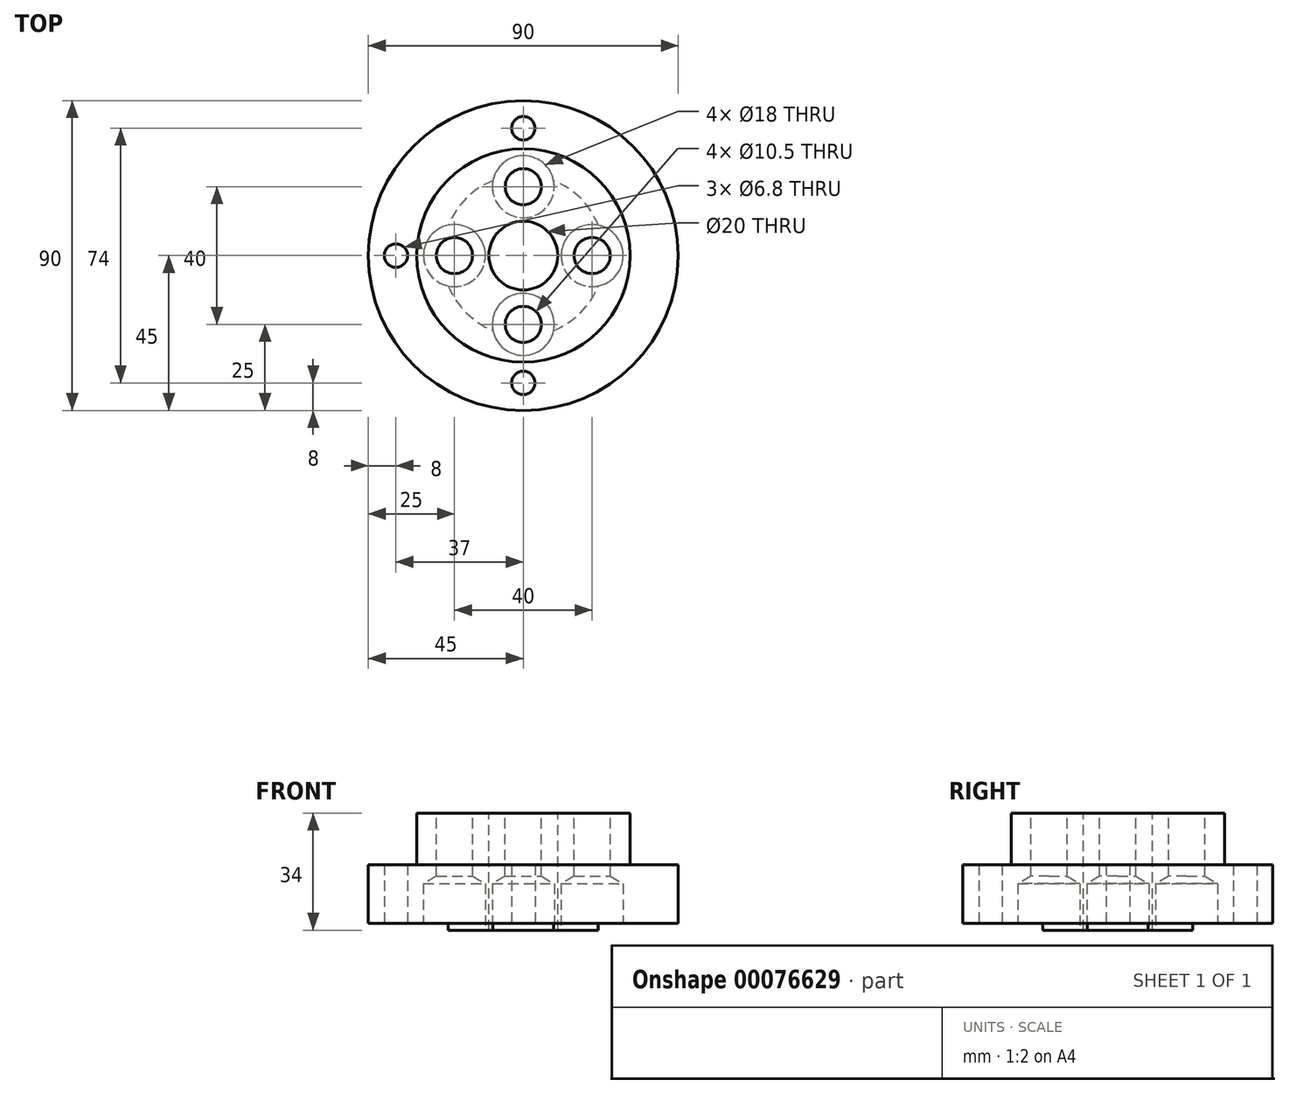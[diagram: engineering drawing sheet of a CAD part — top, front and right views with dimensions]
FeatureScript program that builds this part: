
annotation { "Feature Type Name" : "Feature", "Feature Type Description" : "" }
export const myFeature = defineFeature(function(context is Context, id is Id, definition is map)
    precondition{}
    {
        {
            var Q0;
            Q0=qCreatedBy(makeId("Top.planeOp"),FACE);
            var sketch = newSketch(context, id + "F0", { "sketchPlane" : qUnion([Q0])});
            skCircle(sketch, "E0", {"center": v(0, 0) * mm, "radius": 45 * mm});
            skSolve(sketch);
        }
        {
            var Q0;
            Q0=qSketchRegion(id+"F0",true);
            extrude(context, id + "F1", {"entities" : qUnion([Q0]), "depth" : 17 * mm});
        }
        {
            var Q0;
            Q0=makeQuery(id+"F1.opExtrude","CAP_FACE",FACE,{"disambiguationData":[OSD([sQuery(id+"F0.wireOp",EDGE,"E0")])],"isStart":false});
            var sketch = newSketch(context, id + "F2", { "sketchPlane" : qUnion([Q0])});
            skCircle(sketch, "E1", {"center": v(0, 0) * mm, "radius": 31 * mm});
            skSolve(sketch);
        }
        {
            var Q0;
            Q0=qSketchRegion(id+"F2",true);
            extrude(context, id + "F3", {"entities" : qUnion([Q0]), "operationType" : NewBodyOperationType.ADD, "depth" : 15 * mm});
        }
        {
            var Q0;
            Q0=makeQuery(id+"F3.opExtrude","CAP_FACE",FACE,{"disambiguationData":[OSD([sQuery(id+"F2.wireOp",EDGE,"E1")])],"isStart":false});
            var sketch = newSketch(context, id + "F4", { "sketchPlane" : qUnion([Q0])});
            skCircle(sketch, "E2", {"center": v(0, 0) * mm, "radius": 10 * mm});
            skSolve(sketch);
        }
        {
            var Q0;
            Q0=makeQuery(id+"F3.opExtrude","CAP_FACE",FACE,{"disambiguationData":[OSD([sQuery(id+"F2.wireOp",EDGE,"E1")])],"isStart":false});
            var sketch = newSketch(context, id + "F5", { "sketchPlane" : qUnion([Q0])});
            skCircle(sketch, "E3", {"center": v(20, 0) * mm, "radius": 5.25 * mm});
            skCircle(sketch, "E4", {"center": v(0, -20) * mm, "radius": 5.25 * mm});
            skCircle(sketch, "E5", {"center": v(-20, 0) * mm, "radius": 5.25 * mm});
            skCircle(sketch, "E6", {"center": v(0, 20) * mm, "radius": 5.25 * mm});
            skSolve(sketch);
        }
        {
            var Q0;
            Q0=makeQuery(id+"F1.opExtrude","CAP_FACE",FACE,{"disambiguationData":[OSD([sQuery(id+"F0.wireOp",EDGE,"E0")])],"isStart":true});
            var sketch = newSketch(context, id + "F6", { "sketchPlane" : qUnion([Q0])});
            skCircle(sketch, "E7", {"center": v(0, 0) * mm, "radius": 23.5 * mm});
            skSolve(sketch);
        }
        {
            var Q0;
            Q0=qSketchRegion(id+"F6",true);
            extrude(context, id + "F7", {"entities" : qUnion([Q0]), "operationType" : NewBodyOperationType.ADD, "depth" : 2 * mm});
        }
        {
            var Q0;
            Q0=makeQuery(id+"F7.opExtrude","CAP_FACE",FACE,{"disambiguationData":[OSD([sQuery(id+"F6.wireOp",EDGE,"E7")])],"isStart":false});
            var sketch = newSketch(context, id + "F8", { "sketchPlane" : qUnion([Q0])});
            skCircle(sketch, "E8", {"center": v(0, 20) * mm, "radius": 9 * mm});
            skCircle(sketch, "E9", {"center": v(20, 0) * mm, "radius": 9 * mm});
            skCircle(sketch, "E10", {"center": v(0, -20) * mm, "radius": 9 * mm});
            skCircle(sketch, "E11", {"center": v(-20, 0) * mm, "radius": 9 * mm});
            skSolve(sketch);
        }
        {
            var Q0;
            Q0=sQuery(id+"F8.wireOp",VERTEX,"E11.center");
            var Q1;
            Q1=sQuery(id+"F8.wireOp",VERTEX,"E8.center");
            var Q2;
            Q2=sQuery(id+"F8.wireOp",VERTEX,"E9.center");
            var Q3;
            Q3=sQuery(id+"F8.wireOp",VERTEX,"E10.center");
            var Q4;
            Q4=makeQuery(id+"F1.opExtrude","SWEPT_BODY",BODY,{"disambiguationData":[OSD([sQuery(id+"F0.wireOp",EDGE,"E0")])]});
            hole(context, id + "F9", {"style" : HoleStyle.SIMPLE, "endStyle" : HoleEndStyle.BLIND, "holeDiameter" : 18 * mm, "holeDepth" : 13.5 * mm, "startFromSketch" : true, "locations" : qUnion([Q0, Q1, Q2, Q3]), "scope" : qUnion([Q4])});
        }
        {
            var Q0;
            Q0=sQuery(id+"F4.wireOp",VERTEX,"E2.center");
            var Q1;
            Q1=makeQuery(id+"F1.opExtrude","SWEPT_BODY",BODY,{"disambiguationData":[OSD([sQuery(id+"F0.wireOp",EDGE,"E0")])]});
            hole(context, id + "F10", {"style" : HoleStyle.SIMPLE, "endStyle" : HoleEndStyle.THROUGH, "holeDiameter" : 20 * mm, "startFromSketch" : true, "locations" : qUnion([Q0]), "scope" : qUnion([Q1]), "isTappedThrough" : true});
        }
        {
            var Q0;
            Q0=sQuery(id+"F5.wireOp",VERTEX,"E5.center");
            var Q1;
            Q1=sQuery(id+"F5.wireOp",VERTEX,"E6.center");
            var Q2;
            Q2=sQuery(id+"F5.wireOp",VERTEX,"E3.center");
            var Q3;
            Q3=sQuery(id+"F5.wireOp",VERTEX,"E4.center");
            var Q4;
            Q4=makeQuery(id+"F1.opExtrude","SWEPT_BODY",BODY,{"disambiguationData":[OSD([sQuery(id+"F0.wireOp",EDGE,"E0")])]});
            hole(context, id + "F11", {"style" : HoleStyle.SIMPLE, "endStyle" : HoleEndStyle.THROUGH, "holeDiameter" : 10.5 * mm, "startFromSketch" : true, "locations" : qUnion([Q0, Q1, Q2, Q3]), "scope" : qUnion([Q4]), "isTappedThrough" : true});
        }
        {
            var Q0;
            Q0=makeQuery(id+"F1.opExtrude","CAP_FACE",FACE,{"disambiguationData":[OSD([sQuery(id+"F0.wireOp",EDGE,"E0")])],"isStart":true});
            var sketch = newSketch(context, id + "F12", { "sketchPlane" : qUnion([Q0])});
            skLineSegment(sketch, "E12", {"start": v(0, 0) * mm, "end": v(-37, 0) * mm});
            skLineSegment(sketch, "E13", {"start": v(0, 0) * mm, "end": v(0, 37) * mm});
            skPoint(sketch, "E13.endSnap0", {"position": v(0, 29) * mm});
            skLineSegment(sketch, "E14.MirrorCS", {"start": v(0, 0) * mm, "end": v(37, 0) * mm});
            skLineSegment(sketch, "E15.MirrorCS", {"start": v(0, 0) * mm, "end": v(0, -37) * mm});
            skSolve(sketch);
        }
        {
            var Q0;
            Q0=sQuery(id+"F12.wireOp",VERTEX,"E13.end");
            var Q1;
            Q1=sQuery(id+"F12.wireOp",VERTEX,"E12.end");
            var Q2;
            Q2=sQuery(id+"F12.wireOp",VERTEX,"E15.MirrorCS.end");
            var Q3;
            Q3=sQuery(id+"F12.wireOp",VERTEX,"E14.MirrorCS.end");
            var Q4;
            Q4=makeQuery(id+"F1.opExtrude","SWEPT_BODY",BODY,{"disambiguationData":[OSD([sQuery(id+"F0.wireOp",EDGE,"E0")])]});
            hole(context, id + "F13", {"style" : HoleStyle.SIMPLE, "endStyle" : HoleEndStyle.THROUGH, "holeDiameter" : 6.8 * mm, "startFromSketch" : true, "locations" : qUnion([Q0, Q1, Q2, Q3]), "scope" : qUnion([Q4]), "isTappedThrough" : true});
        }
    });
